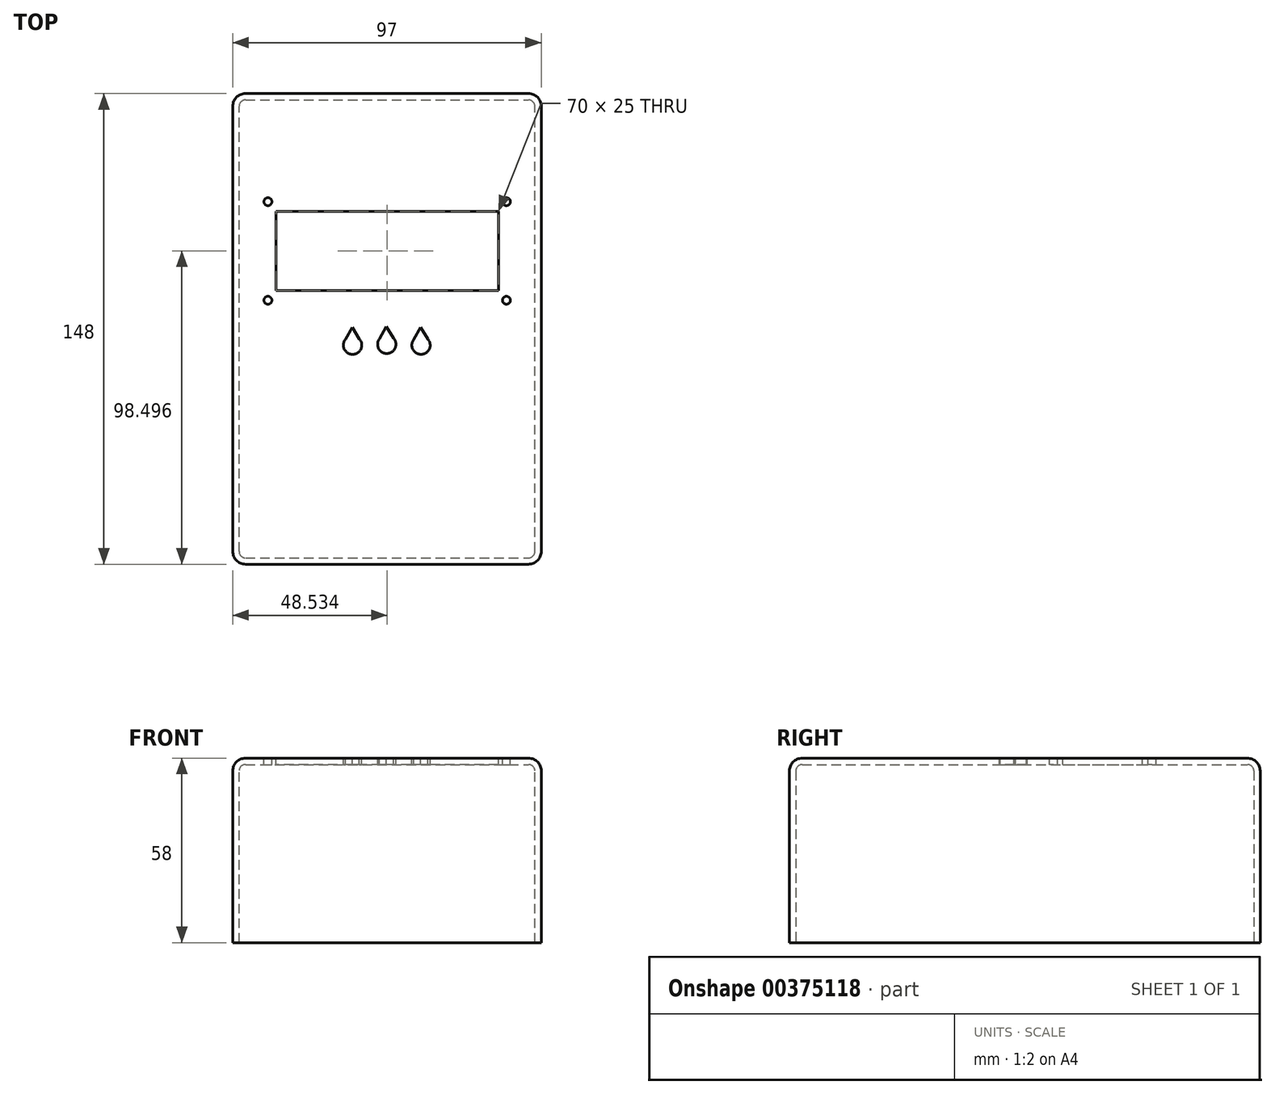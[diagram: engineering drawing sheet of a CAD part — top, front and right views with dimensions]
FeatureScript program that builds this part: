
annotation { "Feature Type Name" : "Feature", "Feature Type Description" : "" }
export const myFeature = defineFeature(function(context is Context, id is Id, definition is map)
    precondition{}
    {
        {
            var Q0;
            Q0=qCreatedBy(makeId("Front.planeOp"),FACE);
            var sketch = newSketch(context, id + "F0", { "sketchPlane" : qUnion([Q0])});
            skLineSegment(sketch, "E0.bottom", {"start": v(70, 29) * mm, "end": v(-70, 29) * mm});
            skLineSegment(sketch, "E0.top", {"start": v(74, -29) * mm, "end": v(-74, -29) * mm});
            skLineSegment(sketch, "E0.left", {"start": v(74, 25) * mm, "end": v(74, -29) * mm});
            skLineSegment(sketch, "E0.right", {"start": v(-74, 25) * mm, "end": v(-74, -29) * mm});
            skPoint(sketch, "E0.middle", {"position": v(0, 0) * mm});
            skPoint(sketch, "E1.visualSharp", {"position": v(-74, 29) * mm});
            skArc(sketch, "E1.filletArc", {"start": v(-70, 29) * mm, "mid": v(-72.83, 27.83) * mm, "end": v(-74, 25) * mm});
            skPoint(sketch, "E2.visualSharp", {"position": v(74, 29) * mm});
            skArc(sketch, "E2.filletArc", {"start": v(74, 25) * mm, "mid": v(72.83, 27.83) * mm, "end": v(70, 29) * mm});
            skSolve(sketch);
        }
        {
            var Q0;
            Q0=makeQuery(id+"F0.imprint","IMPRINT",FACE,{"disambiguationData":[TD([[makeQuery(id+"F0.imprint","IMPRINT",EDGE,{"derivedFrom":sQuery(id+"F0.wireOp",EDGE,"E0.bottom")}),1.0]])]});
            extrude(context, id + "F1", {"entities" : qUnion([Q0]), "endBound" : BoundingType.SYMMETRIC, "depth" : 97 * mm});
        }
        {
            var Q0;
            Q0=makeQuery(id+"F1.opExtrude","CAP_EDGE",EDGE,{"disambiguationData":[OSD([sQuery(id+"F0.wireOp",EDGE,"E2.filletArc")])],"isStart":false});
            fillet(context, id + "F2", {"entities" : qUnion([Q0]), "radius" : 4 * mm, "tangentPropagation" : true, "allowEdgeOverflow" : false});
        }
        {
            var Q0;
            Q0=makeQuery(id+"F1.opExtrude","CAP_EDGE",EDGE,{"disambiguationData":[OSD([sQuery(id+"F0.wireOp",EDGE,"E2.filletArc")])],"isStart":true});
            var Q1;
            Q1=makeQuery(id+"F1.opExtrude","SWEPT_EDGE",EDGE,{"disambiguationData":[OSD([sQuery(id+"F0.wireOp",EDGE,"E0.bottom"),sQuery(id+"F0.wireOp",EDGE,"E2.filletArc")])]});
            fillet(context, id + "F3", {"entities" : qUnion([Q0, Q1]), "radius" : 4 * mm, "tangentPropagation" : true, "allowEdgeOverflow" : false});
        }
        {
            var Q0;
            Q0=makeQuery(id+"F1.opExtrude","SWEPT_FACE",FACE,{"disambiguationData":[OSD([sQuery(id+"F0.wireOp",EDGE,"E0.top")])]});
            shell(context, id + "F4", {"entities" : qUnion([Q0]), "thickness" : 2 * mm});
        }
        {
            var Q0;
            Q0=makeQuery(id+"F1.opExtrude","SWEPT_BODY",BODY,{"disambiguationData":[OSD([sQuery(id+"F0.wireOp",EDGE,"E0.bottom"),sQuery(id+"F0.wireOp",EDGE,"E0.top"),sQuery(id+"F0.wireOp",EDGE,"E0.left"),sQuery(id+"F0.wireOp",EDGE,"E0.right"),sQuery(id+"F0.wireOp",EDGE,"E1.filletArc"),sQuery(id+"F0.wireOp",EDGE,"E2.filletArc")])]});
            var Q1;
            {var subQ0=sQuery(id+"F0.wireOp",EDGE,"E0.left");Q1=makeQuery(id+"F2.opFillet","BLEND_EDGE",EDGE,{"blendedFrom":[makeQuery(id+"F1.opExtrude","CAP_EDGE",EDGE,{"disambiguationData":[OSD([subQ0])],"isStart":false}),makeQuery(id+"F1.opExtrude","SWEPT_FACE",FACE,{"disambiguationData":[OSD([subQ0])]})],"blendedInto":[makeQuery(id+"F1.opExtrude","SWEPT_FACE",FACE,{"disambiguationData":[OSD([subQ0])]})]});}
            transform(context, id + "F5", {"entities" : qUnion([Q0]), "transformType" : TransformType.ROTATION, "transformAxis" : qUnion([Q1]), "angle" : 90 * degree, "makeCopy" : false});
        }
        {
            var Q0;
            Q0=makeQuery(id+"F1.opExtrude","SWEPT_BODY",BODY,{"disambiguationData":[OSD([sQuery(id+"F0.wireOp",EDGE,"E0.bottom"),sQuery(id+"F0.wireOp",EDGE,"E0.top"),sQuery(id+"F0.wireOp",EDGE,"E0.left"),sQuery(id+"F0.wireOp",EDGE,"E0.right"),sQuery(id+"F0.wireOp",EDGE,"E1.filletArc"),sQuery(id+"F0.wireOp",EDGE,"E2.filletArc")])]});
            transform(context, id + "F6", {"entities" : qUnion([Q0]), "transformType" : TransformType.TRANSLATION_3D, "dx" : -118.36 * mm, "dy" : -29.46 * mm, "dz" : 0 * mm, "makeCopy" : false});
        }
        {
            var Q0;
            Q0=makeQuery(id+"F1.opExtrude","SWEPT_FACE",FACE,{"disambiguationData":[OSD([sQuery(id+"F0.wireOp",EDGE,"E0.bottom")])]});
            var sketch = newSketch(context, id + "F7", { "sketchPlane" : qUnion([Q0])});
            skLineSegment(sketch, "E3.bottom", {"start": v(-34.83, 37.04) * mm, "end": v(35.17, 37.04) * mm});
            skLineSegment(sketch, "E3.top", {"start": v(-34.83, 12.04) * mm, "end": v(35.17, 12.04) * mm});
            skLineSegment(sketch, "E3.left", {"start": v(-34.83, 37.04) * mm, "end": v(-34.83, 12.04) * mm});
            skLineSegment(sketch, "E3.right", {"start": v(35.17, 37.04) * mm, "end": v(35.17, 12.04) * mm});
            skSolve(sketch);
        }
        {
            var Q0;
            Q0 = qSketchRegion(id + "F7", true);
            extrude(context, id + "F8", {"entities" : qUnion([Q0]), "operationType" : NewBodyOperationType.REMOVE, "oppositeDirection" : true, "depth" : 25.4 * mm});
        }
        {
            var Q0;
            Q0=makeQuery(id+"F1.opExtrude","SWEPT_FACE",FACE,{"disambiguationData":[OSD([sQuery(id+"F0.wireOp",EDGE,"E0.bottom")])]});
            var sketch = newSketch(context, id + "F9", { "sketchPlane" : qUnion([Q0])});
            skLineSegment(sketch, "E4.bottom", {"start": v(-39.83, 42.54) * mm, "end": v(40.17, 42.54) * mm});
            skLineSegment(sketch, "E4.top", {"start": v(-39.83, 6.54) * mm, "end": v(40.17, 6.54) * mm});
            skLineSegment(sketch, "E4.left", {"start": v(-39.83, 42.54) * mm, "end": v(-39.83, 6.54) * mm});
            skLineSegment(sketch, "E4.right", {"start": v(40.17, 42.54) * mm, "end": v(40.17, 6.54) * mm});
            skCircle(sketch, "E5", {"center": v(-37.33, 40.04) * mm, "radius": 1.24 * mm});
            skCircle(sketch, "E6", {"center": v(-37.33, 9.04) * mm, "radius": 1.24 * mm});
            skCircle(sketch, "E7", {"center": v(37.67, 9.04) * mm, "radius": 1.24 * mm});
            skCircle(sketch, "E8", {"center": v(37.67, 40.04) * mm, "radius": 1.24 * mm});
            skSolve(sketch);
        }
        {
            var Q0;
            Q0=makeQuery(id+"F9.imprint","IMPRINT",FACE,{"disambiguationData":[TD([[makeQuery(id+"F9.imprint","IMPRINT",EDGE,{"derivedFrom":sQuery(id+"F9.wireOp",EDGE,"E8")}),1.0]])]});
            var Q1;
            Q1=sQuery(id+"F9.wireOp",EDGE,"E8");
            extrude(context, id + "F10", {"entities" : qUnion([Q0]), "operationType" : NewBodyOperationType.REMOVE, "surfaceEntities" : qUnion([Q1]), "oppositeDirection" : true, "depth" : 25.4 * mm});
        }
        {
            var Q0;
            Q0=makeQuery(id+"F9.imprint","IMPRINT",FACE,{"disambiguationData":[TD([[makeQuery(id+"F9.imprint","IMPRINT",EDGE,{"derivedFrom":makeQuery(id+"F8.boolean.opBoolean","COPY",EDGE,{"derivedFrom":makeQuery(id+"F8.opExtrude","CAP_EDGE",EDGE,{"disambiguationData":[OSD([sQuery(id+"F7.wireOp",EDGE,"E3.bottom")])],"isStart":true})})}),-1.0]])]});
            var Q1;
            Q1=makeQuery(id+"F9.imprint","IMPRINT",FACE,{"disambiguationData":[TD([[makeQuery(id+"F9.imprint","IMPRINT",EDGE,{"derivedFrom":sQuery(id+"F9.wireOp",EDGE,"E7")}),1.0]])]});
            var Q2;
            Q2=sQuery(id+"F9.wireOp",EDGE,"E7");
            extrude(context, id + "F11", {"entities" : qUnion([Q0, Q1]), "operationType" : NewBodyOperationType.REMOVE, "surfaceEntities" : qUnion([Q2]), "oppositeDirection" : true, "depth" : 25.4 * mm});
        }
        {
            var Q0;
            Q0=makeQuery(id+"F9.imprint","IMPRINT",FACE,{"disambiguationData":[TD([[makeQuery(id+"F9.imprint","IMPRINT",EDGE,{"derivedFrom":sQuery(id+"F9.wireOp",EDGE,"E6")}),1.0]])]});
            var Q1;
            Q1=sQuery(id+"F9.wireOp",EDGE,"E6");
            extrude(context, id + "F12", {"entities" : qUnion([Q0]), "operationType" : NewBodyOperationType.REMOVE, "surfaceEntities" : qUnion([Q1]), "oppositeDirection" : true, "depth" : 25.4 * mm});
        }
        {
            var Q0;
            Q0=makeQuery(id+"F9.imprint","IMPRINT",FACE,{"disambiguationData":[TD([[makeQuery(id+"F9.imprint","IMPRINT",EDGE,{"derivedFrom":sQuery(id+"F9.wireOp",EDGE,"E5")}),1.0]])]});
            var Q1;
            Q1=sQuery(id+"F9.wireOp",EDGE,"E5");
            extrude(context, id + "F13", {"entities" : qUnion([Q0]), "operationType" : NewBodyOperationType.REMOVE, "surfaceEntities" : qUnion([Q1]), "oppositeDirection" : true, "depth" : 25.4 * mm});
        }
        {
            var Q0;
            Q0=makeQuery(id+"F9.imprint","IMPRINT",FACE,{"disambiguationData":[TD([[makeQuery(id+"F9.imprint","IMPRINT",EDGE,{"derivedFrom":sQuery(id+"F9.wireOp",EDGE,"E4.bottom")}),1.0]])]});
            var sketch = newSketch(context, id + "F14", { "sketchPlane" : qUnion([Q0])});
            skCircle(sketch, "E9.cCircle", {"center": v(0.06, -4.84) * mm, "radius": 2.88 * mm});
            skLineSegment(sketch, "E9.0", {"start": v(2.75, -3.82) * mm, "end": v(-2.63, -3.82) * mm});
            skLineSegment(sketch, "E9.1", {"start": v(-2.63, -3.82) * mm, "end": v(-0.06, 0.8) * mm});
            skLineSegment(sketch, "E9.2", {"start": v(-0.06, 0.8) * mm, "end": v(2.75, -3.82) * mm});
            skPoint(sketch, "E9.0.midPoint", {"position": v(0.06, -3.82) * mm});
            skCircle(sketch, "E10.cCircle", {"center": v(-10.7, -5.07) * mm, "radius": 2.88 * mm});
            skLineSegment(sketch, "E10.0", {"start": v(-8, -4.05) * mm, "end": v(-13.4, -4.04) * mm});
            skLineSegment(sketch, "E10.1", {"start": v(-13.4, -4.04) * mm, "end": v(-10.82, 0.58) * mm});
            skLineSegment(sketch, "E10.2", {"start": v(-10.82, 0.58) * mm, "end": v(-8, -4.05) * mm});
            skPoint(sketch, "E10.0.midPoint", {"position": v(-10.7, -4.05) * mm});
            skCircle(sketch, "E11.cCircle", {"center": v(10.82, -5.07) * mm, "radius": 2.88 * mm, "construction": true});
            skLineSegment(sketch, "E11.0", {"start": v(13.51, -4.05) * mm, "end": v(8.12, -4.04) * mm});
            skLineSegment(sketch, "E11.1", {"start": v(8.12, -4.04) * mm, "end": v(10.7, 0.58) * mm});
            skLineSegment(sketch, "E11.2", {"start": v(10.7, 0.58) * mm, "end": v(13.51, -4.05) * mm});
            skPoint(sketch, "E11.0.midPoint", {"position": v(10.82, -4.05) * mm});
            skCircle(sketch, "E12", {"center": v(10.82, -5.07) * mm, "radius": 2.88 * mm});
            skSolve(sketch);
        }
        {
            var Q0;
            Q0 = qSketchRegion(id + "F14", true);
            extrude(context, id + "F15", {"entities" : qUnion([Q0]), "operationType" : NewBodyOperationType.REMOVE, "oppositeDirection" : true, "depth" : 25.4 * mm});
        }
    });
